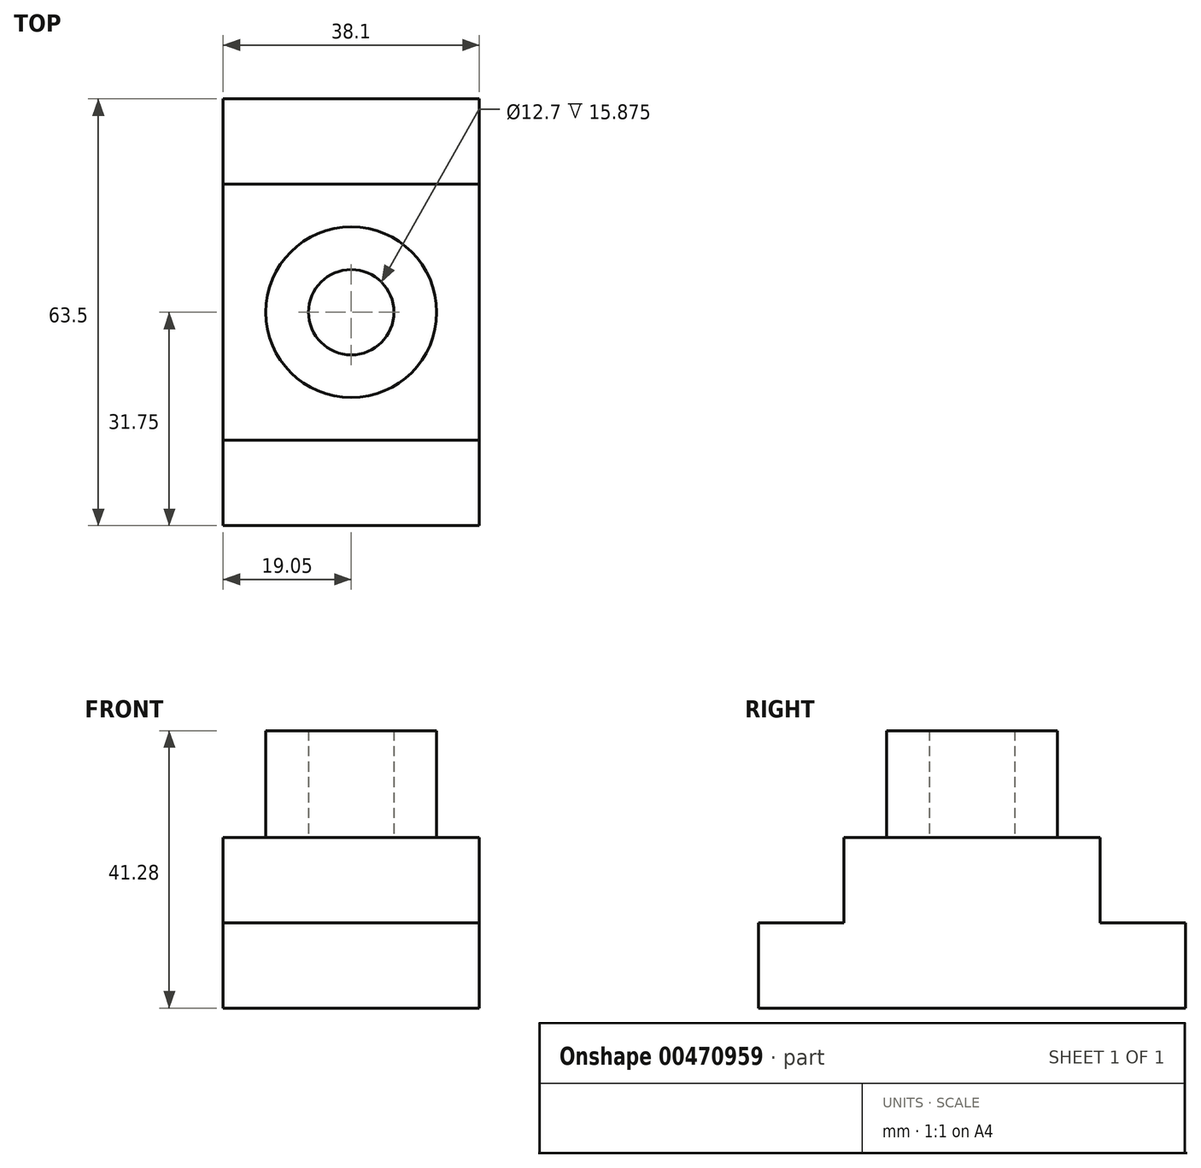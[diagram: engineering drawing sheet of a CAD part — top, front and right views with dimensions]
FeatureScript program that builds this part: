
annotation { "Feature Type Name" : "Feature", "Feature Type Description" : "" }
export const myFeature = defineFeature(function(context is Context, id is Id, definition is map)
    precondition{}
    {
        {
            var Q0;
            Q0=qCreatedBy(makeId("Right.planeOp"),FACE);
            var sketch = newSketch(context, id + "F0", { "sketchPlane" : qUnion([Q0])});
            skLineSegment(sketch, "E0", {"start": v(0, 0) * mm, "end": v(-31.75, 0) * mm});
            skLineSegment(sketch, "E1", {"start": v(-31.75, 0) * mm, "end": v(-31.75, 12.7) * mm});
            skLineSegment(sketch, "E2", {"start": v(-31.75, 12.7) * mm, "end": v(-19.05, 12.7) * mm});
            skLineSegment(sketch, "E3", {"start": v(-19.05, 12.7) * mm, "end": v(-19.05, 25.4) * mm});
            skLineSegment(sketch, "E4", {"start": v(-19.05, 25.4) * mm, "end": v(0, 25.4) * mm});
            skLineSegment(sketch, "E5.MirrorCS", {"start": v(31.75, 0) * mm, "end": v(31.75, 12.7) * mm});
            skLineSegment(sketch, "E6.MirrorCS", {"start": v(31.75, 12.7) * mm, "end": v(19.05, 12.7) * mm});
            skLineSegment(sketch, "E7.MirrorCS", {"start": v(0, 0) * mm, "end": v(31.75, 0) * mm});
            skLineSegment(sketch, "E8.MirrorCS", {"start": v(19.05, 12.7) * mm, "end": v(19.05, 25.4) * mm});
            skLineSegment(sketch, "E9.MirrorCS", {"start": v(19.05, 25.4) * mm, "end": v(0, 25.4) * mm});
            skLineSegment(sketch, "E10", {"start": v(0, 25.4) * mm, "end": v(0, 0) * mm});
            skSolve(sketch);
        }
        {
            var Q0;
            Q0=makeQuery(id+"F0.imprint","IMPRINT",FACE,{"disambiguationData":[TD([[makeQuery(id+"F0.imprint","IMPRINT",EDGE,{"derivedFrom":sQuery(id+"F0.wireOp",EDGE,"E0")}),-1.0]])]});
            var Q1;
            Q1=makeQuery(id+"F0.imprint","IMPRINT",FACE,{"disambiguationData":[TD([[makeQuery(id+"F0.imprint","IMPRINT",EDGE,{"derivedFrom":sQuery(id+"F0.wireOp",EDGE,"E5.MirrorCS")}),1.0]])]});
            extrude(context, id + "F1", {"entities" : qUnion([Q0, Q1]), "depth" : 38.1 * mm});
        }
        {
            var Q0;
            Q0=makeQuery(id+"F1.opExtrude","SWEPT_FACE",FACE,{"disambiguationData":[OSD([sQuery(id+"F0.wireOp",EDGE,"E4"),sQuery(id+"F0.wireOp",EDGE,"E9.MirrorCS")])]});
            var sketch = newSketch(context, id + "F2", { "sketchPlane" : qUnion([Q0])});
            skCircle(sketch, "E11", {"center": v(19.05, 0) * mm, "radius": 12.7 * mm});
            skCircle(sketch, "E12.0", {"center": v(19.05, 0) * mm, "radius": 6.35 * mm});
            skSolve(sketch);
        }
        {
            var Q0;
            Q0 = qSketchRegion(id + "F2", true);
            extrude(context, id + "F3", {"entities" : qUnion([Q0]), "operationType" : NewBodyOperationType.ADD, "depth" : 15.88 * mm});
        }
    });
